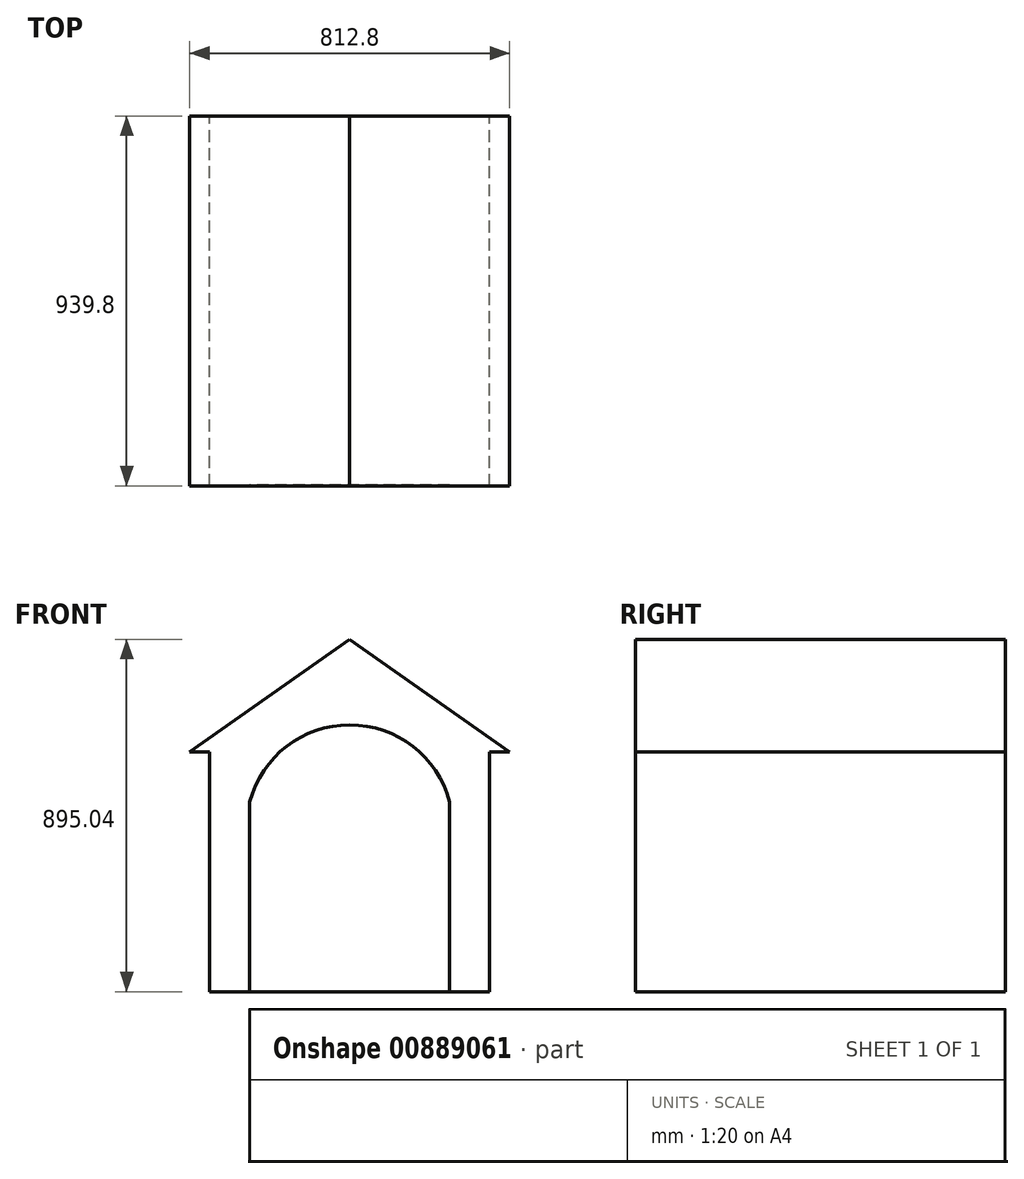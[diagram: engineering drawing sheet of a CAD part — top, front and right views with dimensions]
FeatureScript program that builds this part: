
annotation { "Feature Type Name" : "Feature", "Feature Type Description" : "" }
export const myFeature = defineFeature(function(context is Context, id is Id, definition is map)
    precondition{}
    {
        {
            var Q0;
            Q0=qCreatedBy(makeId("Front.planeOp"),FACE);
            var sketch = newSketch(context, id + "F0", { "sketchPlane" : qUnion([Q0])});
            skLineSegment(sketch, "E0.top", {"start": v(-355.6, -304.8) * mm, "end": v(355.6, -304.8) * mm});
            skLineSegment(sketch, "E0.left", {"start": v(-355.6, 304.8) * mm, "end": v(-355.6, -304.8) * mm});
            skLineSegment(sketch, "E0.right", {"start": v(355.6, 304.8) * mm, "end": v(355.6, -304.8) * mm});
            skPoint(sketch, "E0.middle", {"position": v(0, 0) * mm});
            skLineSegment(sketch, "E1", {"start": v(-406.4, 304.8) * mm, "end": v(-355.6, 304.8) * mm});
            skLineSegment(sketch, "E2", {"start": v(355.6, 304.8) * mm, "end": v(406.4, 304.8) * mm});
            skLineSegment(sketch, "E3", {"start": v(-406.4, 304.8) * mm, "end": v(0, 590.24) * mm});
            skLineSegment(sketch, "E4", {"start": v(0, 590.24) * mm, "end": v(406.4, 304.8) * mm});
            skPoint(sketch, "E5", {"position": v(0, 304.8) * mm});
            skSolve(sketch);
        }
        {
            var Q0;
            Q0 = qSketchRegion(id + "F0", true);
            extrude(context, id + "F1", {"entities" : qUnion([Q0]), "depth" : 939.8 * mm, "offsetDistance" : 25.4 * mm});
        }
        {
            var Q0;
            Q0=makeQuery(id+"F1.opExtrude","CAP_FACE",FACE,{"disambiguationData":[OSD([sQuery(id+"F0.wireOp",EDGE,"E0.top"),sQuery(id+"F0.wireOp",EDGE,"E0.left"),sQuery(id+"F0.wireOp",EDGE,"E0.right"),sQuery(id+"F0.wireOp",EDGE,"E1"),sQuery(id+"F0.wireOp",EDGE,"E2"),sQuery(id+"F0.wireOp",EDGE,"E3"),sQuery(id+"F0.wireOp",EDGE,"E4")])],"isStart":false});
            var sketch = newSketch(context, id + "F2", { "sketchPlane" : qUnion([Q0])});
            skLineSegment(sketch, "E6.bottom", {"start": v(-254, -330.2) * mm, "end": v(254, -330.2) * mm});
            skLineSegment(sketch, "E6.left", {"start": v(-254, -330.2) * mm, "end": v(-254, 177.8) * mm});
            skLineSegment(sketch, "E6.right", {"start": v(254, -330.2) * mm, "end": v(254, 177.8) * mm});
            skArc(sketch, "E7", {"start": v(254, 177.8) * mm, "mid": v(0, 373.16) * mm, "end": v(-254, 177.8) * mm});
            skSolve(sketch);
        }
        {
            var Q0;
            Q0 = qSketchRegion(id + "F2", true);
            extrude(context, id + "F3", {"entities" : qUnion([Q0]), "operationType" : NewBodyOperationType.REMOVE, "oppositeDirection" : true, "depth" : 2.54 * mm, "offsetDistance" : 25.4 * mm});
        }
    });
